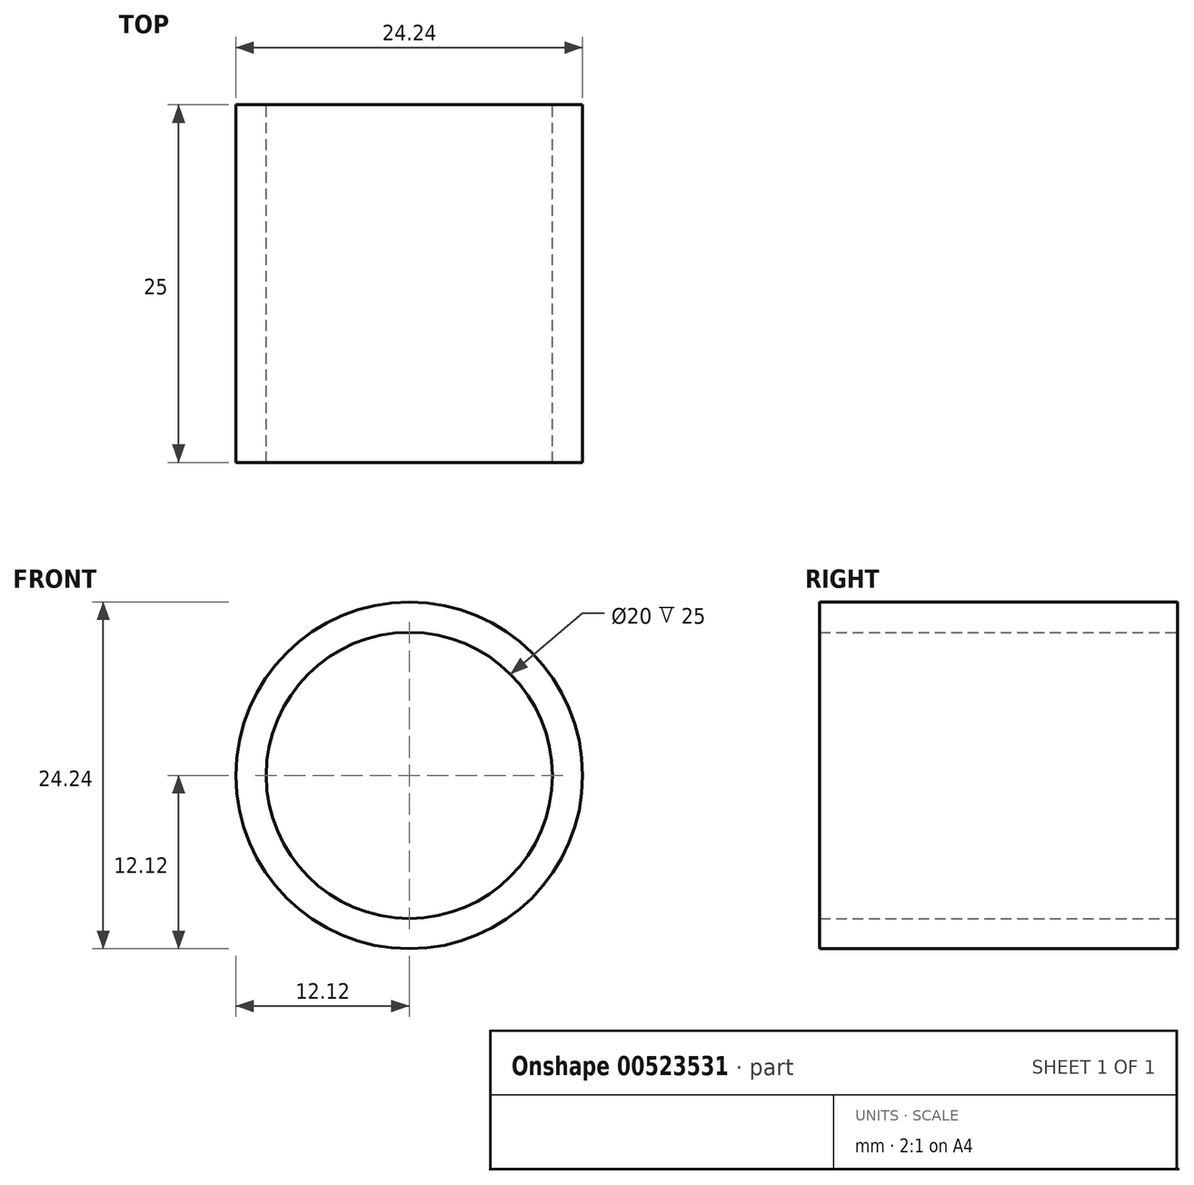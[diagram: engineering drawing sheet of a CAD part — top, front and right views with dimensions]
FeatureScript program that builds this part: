
annotation { "Feature Type Name" : "Feature", "Feature Type Description" : "" }
export const myFeature = defineFeature(function(context is Context, id is Id, definition is map)
    precondition{}
    {
        {
            var Q0;
            Q0=qCreatedBy(makeId("Front.planeOp"),FACE);
            var sketch = newSketch(context, id + "F0", { "sketchPlane" : qUnion([Q0])});
            skCircle(sketch, "E0", {"center": v(0, 0) * mm, "radius": 12.12 * mm});
            skCircle(sketch, "E1", {"center": v(0, 0) * mm, "radius": 10 * mm});
            skSolve(sketch);
        }
        {
            var Q0;
            Q0 = qSketchRegion(id + "F0", true);
            extrude(context, id + "F1", {"entities" : qUnion([Q0]), "depth" : 25 * mm, "offsetDistance" : 25 * mm});
        }
    });
